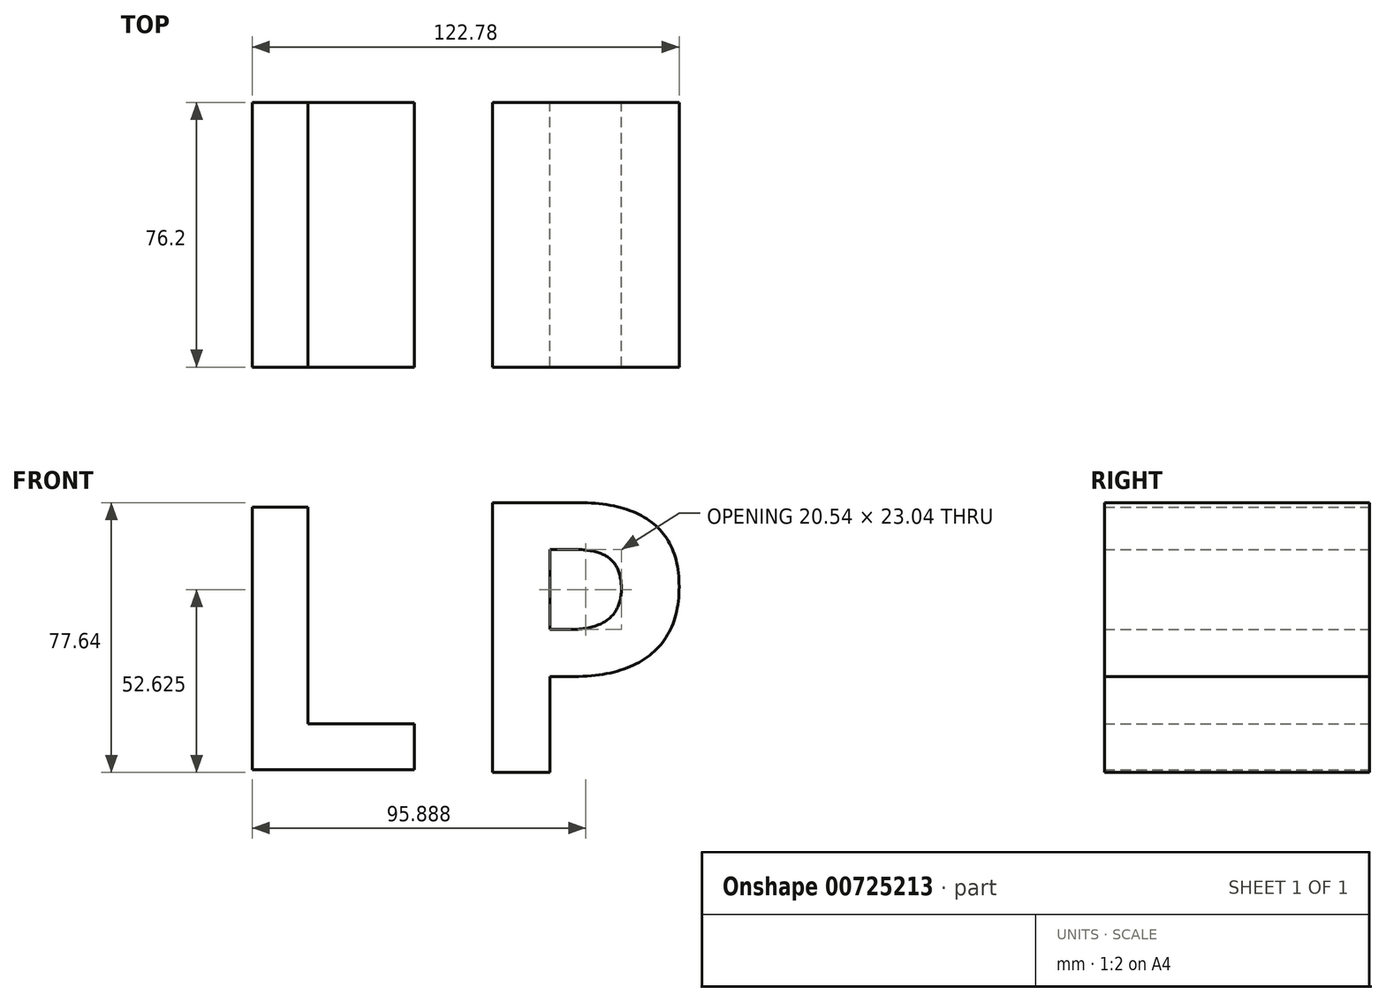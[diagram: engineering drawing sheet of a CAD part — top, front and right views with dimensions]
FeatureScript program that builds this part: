
annotation { "Feature Type Name" : "Feature", "Feature Type Description" : "" }
export const myFeature = defineFeature(function(context is Context, id is Id, definition is map)
    precondition{}
    {
        {
            var Q0;
            Q0=qCreatedBy(makeId("Front.planeOp"),FACE);
            var sketch = newSketch(context, id + "F0", { "sketchPlane" : qUnion([Q0])});
            skText(sketch, "E0", { "text": "MLP\n", "fontName": "OpenSans-Bold.ttf"});
            const initialGuessF0  = {"E0": [-0.11462, -0.03555, 1, 0, 0.0762]};
            skSetInitialGuess(sketch, initialGuessF0);
            skSolve(sketch);
        }
        {
            var Q0;
            Q0=makeQuery(id+"F0.imprint","IMPRINT",FACE,{"disambiguationData":[TD([[makeQuery(id+"F0.imprint","IMPRINT",EDGE,{"derivedFrom":sQuery(id+"F0.wireOp",EDGE,"E0.sketch_text.stroke-0")}),-1.0]])]});
            var sketch = newSketch(context, id + "F1", { "sketchPlane" : qUnion([Q0])});
            skSolve(sketch);
        }
        {
            var Q0;
            Q0=makeQuery(id+"F1.imprint","IMPRINT",FACE,{"disambiguationData":[TD([[makeQuery(id+"F1.imprint","IMPRINT",EDGE,{"derivedFrom":makeQuery(id+"F0.imprint","IMPRINT",EDGE,{"derivedFrom":sQuery(id+"F0.wireOp",EDGE,"E0.sketch_text.stroke-0")})}),-1.0]])]});
            var Q1;
            Q1=makeQuery(id+"F0.imprint","IMPRINT",FACE,{"disambiguationData":[TD([[makeQuery(id+"F0.imprint","IMPRINT",EDGE,{"derivedFrom":sQuery(id+"F0.wireOp",EDGE,"E0.sketch_text.stroke-19")}),-1.0]])]});
            extrude(context, id + "F2", {"entities" : qUnion([Q0, Q1]), "endBound" : BoundingType.SYMMETRIC, "depth" : 76.2 * mm, "offsetDistance" : 25.4 * mm});
        }
        {
            var Q0;
            Q0=qCreatedBy(makeId("Front.planeOp"),FACE);
            var sketch = newSketch(context, id + "F3", { "sketchPlane" : qUnion([Q0])});
            skText(sketch, "E1", { "text": "P", "fontName": "OpenSans-Bold.ttf"});
            const initialGuessF3  = {"E1": [0.05405, -0.03634, 1, 0, 0.0783]};
            skSetInitialGuess(sketch, initialGuessF3);
            skSolve(sketch);
        }
        {
            var Q0;
            Q0 = qSketchRegion(id + "F3", true);
            extrude(context, id + "F4", {"entities" : qUnion([Q0]), "endBound" : BoundingType.SYMMETRIC, "depth" : 76.2 * mm, "offsetDistance" : 25.4 * mm});
        }
    });
